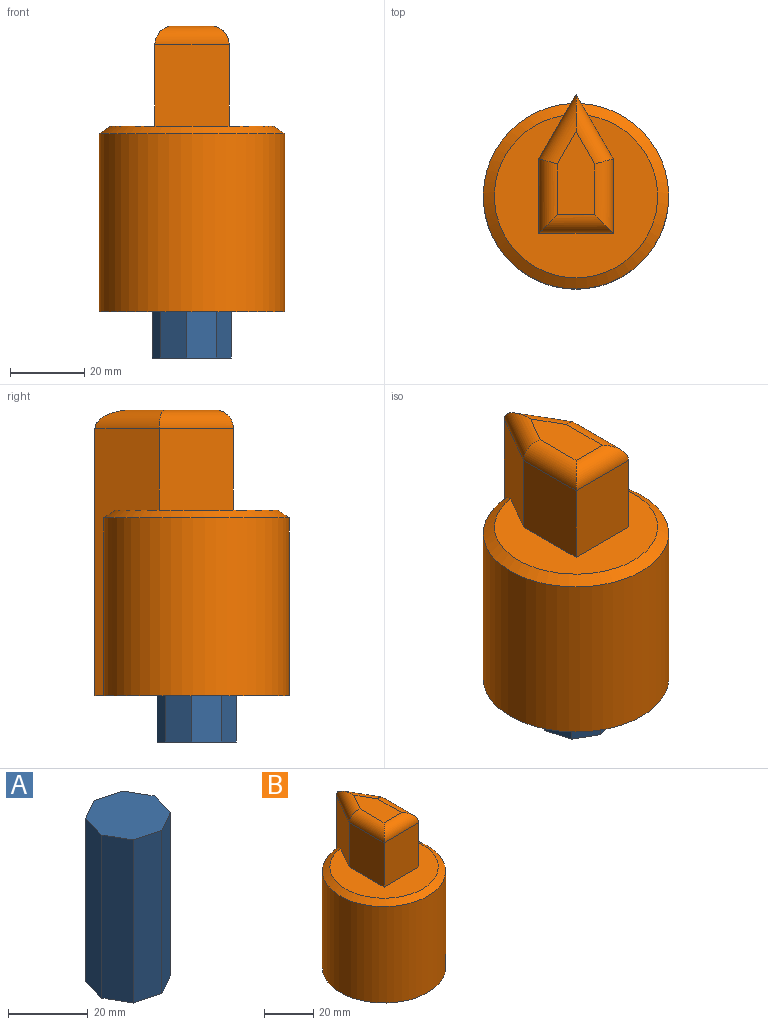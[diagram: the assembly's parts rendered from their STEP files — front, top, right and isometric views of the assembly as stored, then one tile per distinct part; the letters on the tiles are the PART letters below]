
ASSEMBLY  parts=2 mates=1
PART A: 10 faces, bbox 21.2x21.2x50 mm
  f0: plane 50x7.92mm, normal (0.26,0.97,0), area 410.1mm2, adj f1,f7,f8,f9
  f1: plane 50x7.1mm, normal (-0.5,0.87,0), area 410.1mm2, adj f0,f2,f8,f9
  f2: plane 50x7.92mm, normal (-0.97,0.26,0), area 410.1mm2, adj f1,f3,f8,f9
  f3: plane 50x7.1mm, normal (-0.87,-0.5,0), area 410.1mm2, adj f2,f4,f8,f9
  f4: plane 50x7.92mm, normal (-0.26,-0.97,0), area 410.1mm2, adj f3,f5,f8,f9
  f5: plane 50x7.1mm, normal (0.5,-0.87,0), area 410.1mm2, adj f4,f6,f8,f9
  f6: plane 50x7.92mm, normal (0.97,-0.26,0), area 410.1mm2, adj f5,f7,f8,f9
  f7: plane 50x7.1mm, normal (0.87,0.5,0), area 410.1mm2, adj f0,f6,f8,f9
  f8: plane 21.25x21.25mm, normal (0,0,-1), area 324.8mm2, adj f0,f1,f2,f3,f4,f5,f6,f7
  f9: plane 21.25x21.25mm, normal (0,0,1), area 324.8mm2, adj f0,f1,f2,f3,f4,f5,f6,f7
PART B: 24 faces, bbox 50x52.3x77 mm
  f0: cylinder r=25mm len=50mm, axis (0,0,-1), area 7393.6mm2, adj f2,f3,f4,f14
  f1: plane 44x43.77mm, normal (0,0,1), area 964.1mm2, adj f3,f4,f5,f6,f7,f14
  f2: plane 52.32x50mm, normal (0,0,-1), area 1635.3mm2, adj f0,f3,f4,f15,f16,f17,f18,f19
  f3: plane 72x17.32mm, normal (-0.87,0.5,0), area 580mm2, adj f0,f1,f2,f4,f5,f9,f14
  f4: plane 72x17.32mm, normal (0.87,0.5,0), area 580mm2, adj f0,f1,f2,f3,f7,f10,f14
  f5: plane 22x20mm, normal (-1,0,0), area 440mm2, adj f1,f3,f6,f11
  f6: plane 22x20mm, normal (0,-1,0), area 440mm2, adj f1,f5,f7,f13
  f7: plane 22x20mm, normal (1,0,0), area 440mm2, adj f1,f4,f6,f12
  f8: plane 22.32x10mm, normal (0,0,1), area 179.9mm2, adj f9,f10,f11,f12,f13
  f9: cylinder r=5mm len=19.82mm, axis (-0.5,-0.87,0), area 128.5mm2, adj f3,f8,f10,f11
  f10: cylinder r=5mm len=19.82mm, axis (-0.5,0.87,0), area 128.5mm2, adj f4,f8,f9,f12
  f11: cylinder r=5mm len=20mm, axis (0,-1,0), area 139mm2, adj f5,f8,f9,f13
  f12: cylinder r=5mm len=20mm, axis (0,1,0), area 139mm2, adj f7,f8,f10,f13
  f13: cylinder r=5mm len=20mm, axis (1,0,0), area 128.5mm2, adj f6,f8,f11,f12
  f14: cone r=22mm half-angle=55deg, axis (0,0,-1), area 524.1mm2, adj f0,f1,f3,f4
  f15: plane 25x7.98mm, normal (0.27,-0.96,0), area 207.1mm2, adj f2,f16,f22,f23
  f16: plane 25x7.21mm, normal (-0.49,-0.87,0), area 207.1mm2, adj f2,f15,f17,f23
  f17: plane 25x7.98mm, normal (-0.96,-0.27,0), area 207.1mm2, adj f2,f16,f18,f23
  f18: plane 25x7.21mm, normal (-0.87,0.49,0), area 207.1mm2, adj f2,f17,f19,f23
  f19: plane 25x7.98mm, normal (-0.27,0.96,0), area 207.1mm2, adj f2,f18,f20,f23
  f20: plane 25x7.21mm, normal (0.49,0.87,0), area 207.1mm2, adj f2,f19,f21,f23
  f21: plane 25x7.98mm, normal (0.96,0.27,0), area 207.1mm2, adj f2,f20,f22,f23
  f22: plane 25x7.21mm, normal (0.87,-0.49,0), area 207.1mm2, adj f2,f15,f21,f23
  f23: plane 21.49x21.49mm, normal (0,0,-1), area 331.4mm2, adj f15,f16,f17,f18,f19,f20,f21,f22
PLACE A rot(axis=(0,0,-1),59.5deg) t=(-12.81,-1.39,51.8)mm
PLACE B t=(-12.76,-1.3,14.3)mm
MATE parallel A.f5 <-> B.f20  axis (-0.49,-0.87,0) through (-17.68,-10,26.8)mm
